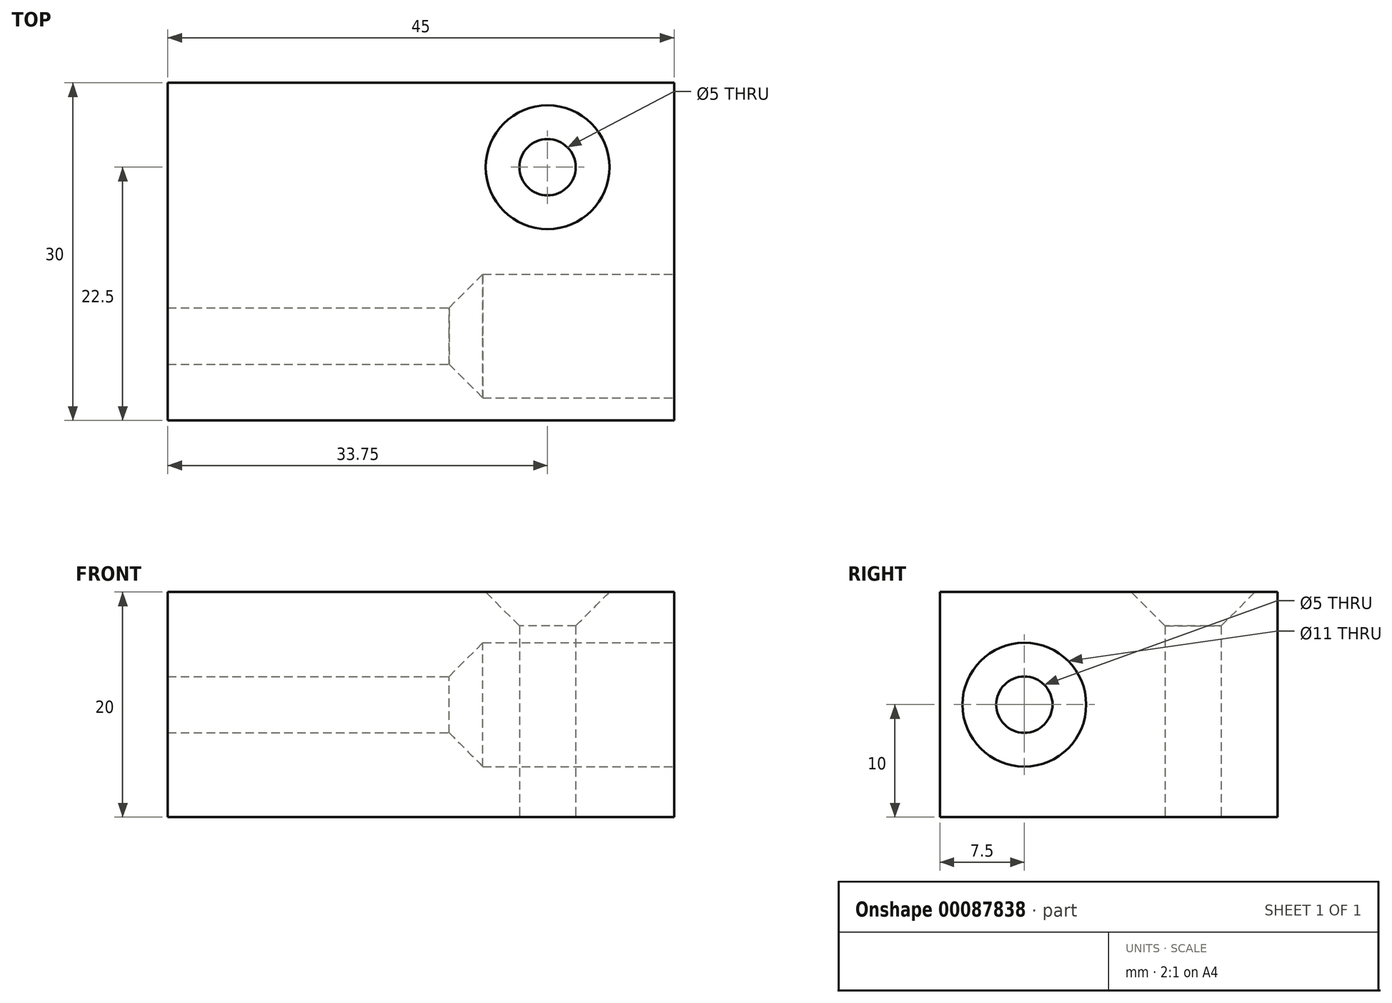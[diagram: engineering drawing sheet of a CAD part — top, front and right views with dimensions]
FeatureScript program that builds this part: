
annotation { "Feature Type Name" : "Feature", "Feature Type Description" : "" }
export const myFeature = defineFeature(function(context is Context, id is Id, definition is map)
    precondition{}
    {
        {
            var Q0;
            Q0=qCreatedBy(makeId("Top.planeOp"),FACE);
            var sketch = newSketch(context, id + "F0", { "sketchPlane" : qUnion([Q0])});
            skLineSegment(sketch, "E0.bottom", {"start": v(22.5, 15) * mm, "end": v(-22.5, 15) * mm});
            skLineSegment(sketch, "E0.top", {"start": v(22.5, -15) * mm, "end": v(-22.5, -15) * mm});
            skLineSegment(sketch, "E0.left", {"start": v(22.5, 15) * mm, "end": v(22.5, -15) * mm});
            skLineSegment(sketch, "E0.right", {"start": v(-22.5, 15) * mm, "end": v(-22.5, -15) * mm});
            skPoint(sketch, "E0.middle", {"position": v(0, 0) * mm});
            skCircle(sketch, "E1", {"center": v(11.25, 7.5) * mm, "radius": 2.5 * mm});
            skLineSegment(sketch, "E2", {"start": v(22.5, 15) * mm, "end": v(0, 0) * mm, "construction": true});
            skSolve(sketch);
        }
        {
            var Q0;
            Q0=makeQuery(id+"F0.imprint","IMPRINT",FACE,{"disambiguationData":[TD([[makeQuery(id+"F0.imprint","IMPRINT",EDGE,{"derivedFrom":sQuery(id+"F0.wireOp",EDGE,"E0.bottom")}),1.0]])]});
            extrude(context, id + "F1", {"entities" : qUnion([Q0]), "depth" : 20 * mm});
        }
        {
            var Q0;
            Q0=makeQuery(id+"F1.opExtrude","SWEPT_FACE",FACE,{"disambiguationData":[OSD([sQuery(id+"F0.wireOp",EDGE,"E0.left")])]});
            var sketch = newSketch(context, id + "F2", { "sketchPlane" : qUnion([Q0])});
            skCircle(sketch, "E3", {"center": v(-7.5, 10) * mm, "radius": 2.5 * mm});
            skLineSegment(sketch, "E4", {"start": v(15, 10) * mm, "end": v(-15, 10) * mm, "construction": true});
            skLineSegment(sketch, "E5", {"start": v(0, 10) * mm, "end": v(-15, 10) * mm, "construction": true});
            skCircle(sketch, "E6", {"center": v(-7.5, 10) * mm, "radius": 5.5 * mm});
            skSolve(sketch);
        }
        {
            var Q0;
            Q0=makeQuery(id+"F2.imprint","IMPRINT",FACE,{"disambiguationData":[TD([[makeQuery(id+"F2.imprint","IMPRINT",EDGE,{"derivedFrom":sQuery(id+"F2.wireOp",EDGE,"E3")}),1.0]])]});
            extrude(context, id + "F3", {"entities" : qUnion([Q0]), "operationType" : NewBodyOperationType.REMOVE, "endBound" : BoundingType.THROUGH_ALL, "oppositeDirection" : true, "depth" : 25 * mm});
        }
        {
            var Q0;
            Q0=makeQuery(id+"F2.imprint","IMPRINT",FACE,{"disambiguationData":[TD([[makeQuery(id+"F2.imprint","IMPRINT",EDGE,{"derivedFrom":sQuery(id+"F2.wireOp",EDGE,"E3")}),-1.0]])]});
            extrude(context, id + "F4", {"entities" : qUnion([Q0]), "operationType" : NewBodyOperationType.REMOVE, "oppositeDirection" : true, "depth" : 20 * mm});
        }
        {
            var Q0;
            Q0=makeQuery(id+"F1.opExtrude","CAP_EDGE",EDGE,{"disambiguationData":[OSD([sQuery(id+"F0.wireOp",EDGE,"E1")])],"isStart":false});
            var Q1;
            Q1=makeQuery(id+"F4.boolean.opBoolean","COPY",EDGE,{"derivedFrom":makeQuery(id+"F4.opExtrude","CAP_EDGE",EDGE,{"disambiguationData":[OSD([sQuery(id+"F2.wireOp",EDGE,"E6")])],"isStart":false})});
            chamfer(context, id + "F5", {"entities" : qUnion([Q0, Q1]), "width" : 3 * mm, "tangentPropagation" : true});
        }
    });
